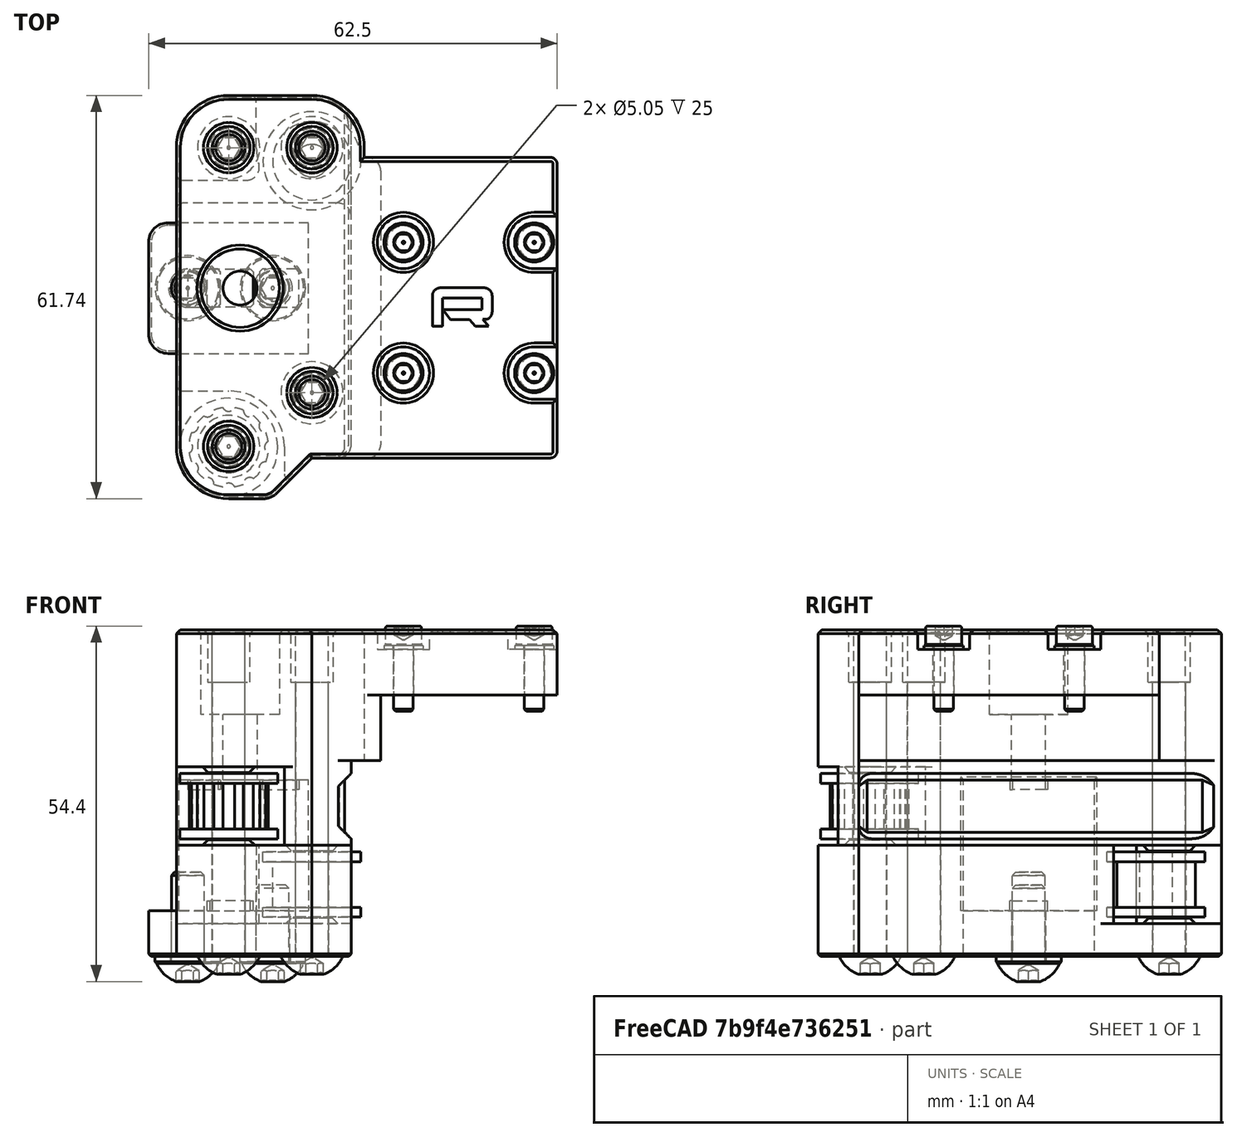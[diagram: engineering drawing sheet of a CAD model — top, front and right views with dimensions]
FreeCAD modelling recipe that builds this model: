
FCSTD DOCUMENT  (FreeCAD 0.19R24291 (Git))
Label: y-carrier-right-assembly
License: Other
LicenseURL: GPL3
objects: Part::FeaturePython×16, Part::Feature×4, App::Part×1
note: 20 computed .brp shape members not serialized (recipe doc carries the construction recipe); baked Part::Feature solids carry a one-line shape summary decoded from their .brp

FEATURE [Part::Feature] Part__Mirroring002001  label="20t-idler"
  Placement = pos=(0,-4.61,0) rot=(0,0,1;0rad)
  shape: bbox 15 x 15 x 10 mm, 31 faces (baked)
FEATURE [Part::Feature] Part__Mirroring003001  label="smooth-idler"
  Placement = pos=(2,0.5,0) rot=(0,0,1;0rad)
  shape: bbox 15 x 15 x 10 mm, 8 faces (baked)
FEATURE [Part::Feature] Chamfer008001
  Placement = pos=(0,0,3) rot=(0,0,1;0rad)
  shape: bbox 31 x 61.74 x 17.85 mm, 86 faces (baked)
FEATURE [Part::FeaturePython] Washer  label="M5-Washer"  # Fasteners workbench fastener (typed FeaturePython)
  Placement = pos=(-28,0,3) rot=(-1,0,0;3.14159rad)
  baseObject = -> Chamfer008001 [Edge76]
  diameter = 1
  invert = false
  matchOuter = true
  offset = 0
  type = 4
FEATURE [Part::FeaturePython] Screw  label="M5x14-Screw"  # Fasteners workbench fastener (typed FeaturePython)
  Placement = pos=(-28,1e-16,1.9) rot=(-1,0,0;3.14159rad)
  baseObject = -> Washer [Edge1]
  diameter = 3
  invert = false
  length = 3
  lengthCustom = 14
  matchOuter = true
  offset = 0
  thread = false
  type = 39
FEATURE [Part::FeaturePython] Washer001  label="M5-Washer001"  # Fasteners workbench fastener (typed FeaturePython)
  Placement = pos=(-15,0,3) rot=(-1,0,0;3.14159rad)
  baseObject = -> Chamfer008001 [Edge80]
  diameter = 1
  invert = false
  matchOuter = true
  offset = 0
  type = 4
FEATURE [Part::FeaturePython] Screw001  label="M5x12-Screw"  # Fasteners workbench fastener (typed FeaturePython)
  Placement = pos=(-15,1e-16,1.9) rot=(-1,0,0;3.14159rad)
  baseObject = -> Washer001 [Edge1]
  diameter = 3
  invert = false
  length = 2
  lengthCustom = 12
  matchOuter = true
  offset = 0
  thread = false
  type = 39
FEATURE [Part::Feature] Cut002
  Placement = pos=(0,0,3) rot=(0,0,1;0rad)
  shape: bbox 58.24 x 61.74 x 33.85 mm, 150 faces (baked)
FEATURE [Part::FeaturePython] Screw002  label="M5x50-Screw"  # Fasteners workbench fastener (typed FeaturePython)
  Placement = pos=(-9,21.5,3) rot=(-1,0,0;3.14159rad)
  baseObject = -> Chamfer008001 [Edge84]
  diameter = 3
  invert = false
  length = 11
  lengthCustom = 50
  matchOuter = true
  offset = 0
  thread = false
  type = 39
FEATURE [Part::FeaturePython] Screw003  label="M5x50-Screw001"  # Fasteners workbench fastener (typed FeaturePython)
  Placement = pos=(-21.74,21.5,3) rot=(-1,0,0;3.14159rad)
  baseObject = -> Chamfer008001 [Edge82]
  diameter = 3
  invert = false
  length = 11
  lengthCustom = 50
  matchOuter = true
  offset = 0
  thread = false
  type = 39
FEATURE [Part::FeaturePython] Screw004  label="M5x50-Screw002"  # Fasteners workbench fastener (typed FeaturePython)
  Placement = pos=(-9,-16,3) rot=(-1,0,0;3.14159rad)
  baseObject = -> Chamfer008001 [Edge81]
  diameter = 3
  invert = false
  length = 11
  lengthCustom = 50
  matchOuter = true
  offset = 0
  thread = false
  type = 39
FEATURE [Part::FeaturePython] Screw005  label="M5x50-Screw003"  # Fasteners workbench fastener (typed FeaturePython)
  Placement = pos=(-21.74,-24.24,3) rot=(-1,0,0;3.14159rad)
  baseObject = -> Chamfer008001 [Edge83]
  diameter = 3
  invert = false
  length = 11
  lengthCustom = 50
  matchOuter = true
  offset = 0
  thread = false
  type = 39
FEATURE [Part::FeaturePython] Washer002  label="M3-Washer"  # Fasteners workbench fastener (typed FeaturePython)
  Placement = pos=(25,7,50) rot=(0,0,1;0rad)
  baseObject = -> Cut002 [Edge375]
  diameter = 4
  invert = true
  matchOuter = true
  offset = 0
  type = 5
FEATURE [Part::FeaturePython] Washer003  label="M3-Washer004"  # Fasteners workbench fastener (typed FeaturePython)
  Placement = pos=(25,-13,50) rot=(0,0,1;0rad)
  baseObject = -> Cut002 [Edge371]
  diameter = 4
  invert = true
  matchOuter = true
  offset = 0
  type = 5
FEATURE [Part::FeaturePython] Washer004  label="M3-Washer005"  # Fasteners workbench fastener (typed FeaturePython)
  Placement = pos=(5,-13,50) rot=(0,0,1;0rad)
  baseObject = -> Cut002 [Edge369]
  diameter = 4
  invert = true
  matchOuter = true
  offset = 0
  type = 5
FEATURE [Part::FeaturePython] Washer005  label="M3-Washer006"  # Fasteners workbench fastener (typed FeaturePython)
  Placement = pos=(5,7,50) rot=(0,0,1;0rad)
  baseObject = -> Cut002 [Edge373]
  diameter = 4
  invert = true
  matchOuter = true
  offset = 0
  type = 5
FEATURE [Part::FeaturePython] Screw006  label="M3x10-Screw"  # Fasteners workbench fastener (typed FeaturePython)
  Placement = pos=(25,-13,50.55) rot=(0,0,1;0rad)
  baseObject = -> Washer003 [Edge1]
  diameter = 4
  invert = false
  length = 3
  lengthCustom = 10
  matchOuter = true
  offset = 0
  thread = false
  type = 33
FEATURE [Part::FeaturePython] Screw007  label="M3x10-Screw001"  # Fasteners workbench fastener (typed FeaturePython)
  Placement = pos=(5,-13,50.55) rot=(0,0,1;0rad)
  baseObject = -> Washer004 [Edge1]
  diameter = 4
  invert = false
  length = 3
  lengthCustom = 10
  matchOuter = true
  offset = 0
  thread = false
  type = 33
FEATURE [Part::FeaturePython] Screw008  label="M3x10-Screw002"  # Fasteners workbench fastener (typed FeaturePython)
  Placement = pos=(5,7,50.55) rot=(0,0,1;0rad)
  baseObject = -> Washer005 [Edge1]
  diameter = 4
  invert = false
  length = 3
  lengthCustom = 10
  matchOuter = true
  offset = 0
  thread = false
  type = 33
FEATURE [Part::FeaturePython] Screw009  label="M3x10-Screw003"  # Fasteners workbench fastener (typed FeaturePython)
  Placement = pos=(25,7,50.55) rot=(0,0,1;0rad)
  baseObject = -> Washer002 [Edge1]
  diameter = 4
  invert = false
  length = 3
  lengthCustom = 10
  matchOuter = true
  offset = 0
  thread = false
  type = 33
FEATURE [App::Part] Part  label="Y-carrier-right"
  Group = -> [Part__Mirroring002001,Part__Mirroring003001,Chamfer008001,Cut002,Washer001,Screw,Screw001,Washer,Screw003,Screw004,Screw005,Screw002,Screw006,Screw009,Screw008,Screw007,Washer005,Washer004,Washer003,Washer002]
  Origin = -> Origin
